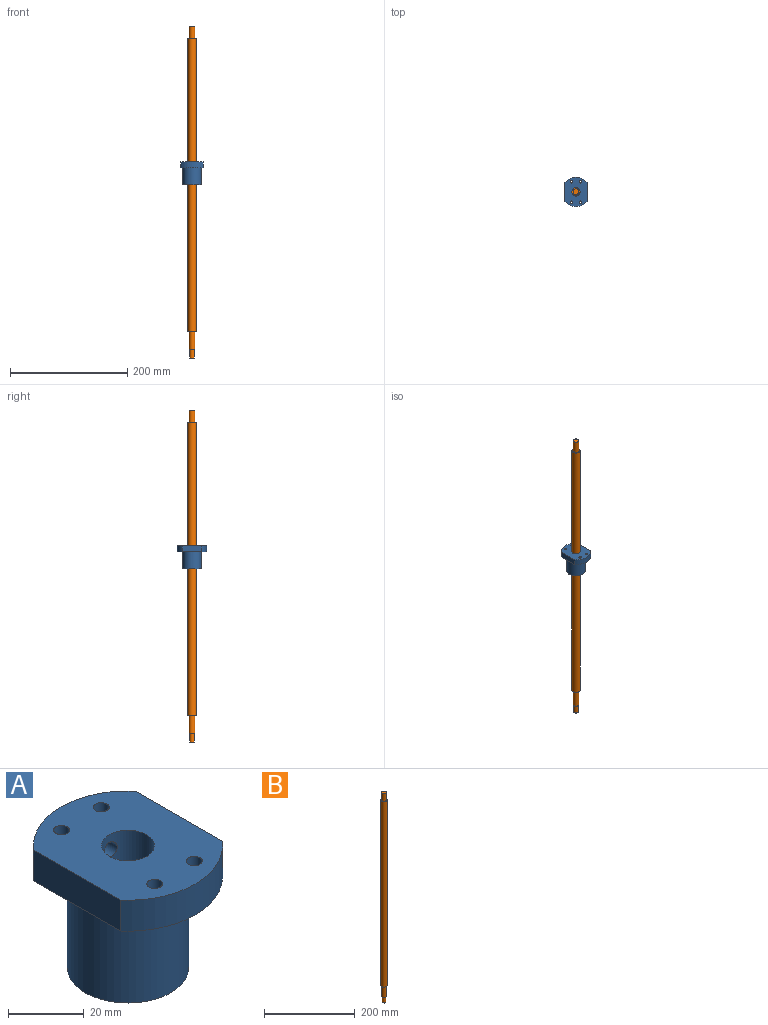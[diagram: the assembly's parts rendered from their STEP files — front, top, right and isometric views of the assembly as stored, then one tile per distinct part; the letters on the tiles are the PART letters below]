
ASSEMBLY  parts=2 mates=1
PART A: 14 faces, bbox 38x50x39.6 mm
  f0: cylinder r=7mm len=39.6mm, axis (0,0,-1), area 1721.8mm2, adj f2,f11,f13
  f1: cylinder r=16mm len=32mm, axis (0,0,-1), area 2975.7mm2, adj f2,f12
  f2: plane 32x32mm, normal (0,0,-1), area 650.3mm2, adj f0,f1
  f3: plane 32.5x10mm, normal (-1,0,0), area 325mm2, adj f4,f6,f11,f12
  f4: cylinder r=25mm len=38mm, axis (0,0,-1), area 431.7mm2, adj f3,f5,f11,f12
  f5: plane 32.5x10mm, normal (1,0,0), area 325mm2, adj f4,f6,f11,f12
  f6: cylinder r=25mm len=38mm, axis (0,0,-1), area 412mm2, adj f3,f5,f11,f12,f13
  f7: cylinder r=2.1mm len=10mm, axis (0,0,-1), area 131.9mm2, adj f11,f12
  f8: cylinder r=2.1mm len=10mm, axis (0,0,-1), area 131.9mm2, adj f11,f12
  f9: cylinder r=2.1mm len=10mm, axis (0,0,-1), area 131.9mm2, adj f11,f12
  f10: cylinder r=2.1mm len=10mm, axis (0,0,-1), area 131.9mm2, adj f11,f12
  f11: plane 50x38mm, normal (0,0,1), area 1487.2mm2, adj f0,f3,f4,f5,f6,f7,f8,f9
  f12: plane 50x38mm, normal (0,0,-1), area 836.9mm2, adj f1,f3,f4,f5,f6,f7,f8,f9
  f13: cylinder r=2.5mm len=18.46mm, axis (0,-1,0), area 285.3mm2, adj f0,f6
PART B: 9 faces, bbox 14x14x566 mm
  f0: cylinder r=4mm len=15mm, axis (0,0,-1), area 377mm2, adj f1,f3
  f1: plane 8x8mm, normal (0,0,-1), area 50.3mm2, adj f0
  f2: cylinder r=5mm len=30mm, axis (0,0,-1), area 942.5mm2, adj f3,f6
  f3: plane 10x10mm, normal (0,0,-1), area 28.3mm2, adj f0,f2
  f4: cylinder r=7mm len=500mm, axis (0,0,-1), area 21991.1mm2, adj f5,f6
  f5: plane 14x14mm, normal (0,0,1), area 75.4mm2, adj f4,f7
  f6: plane 14x14mm, normal (0,0,-1), area 75.4mm2, adj f2,f4
  f7: cylinder r=5mm len=21mm, axis (0,0,-1), area 659.7mm2, adj f5,f8
  f8: plane 10x10mm, normal (0,0,1), area 78.5mm2, adj f7
PLACE A t=(0,0,-250)mm
PLACE B at identity
MATE cylindrical A.f0 <-> B.f4  axis (0,0,-1) through (0,0,295)mm
